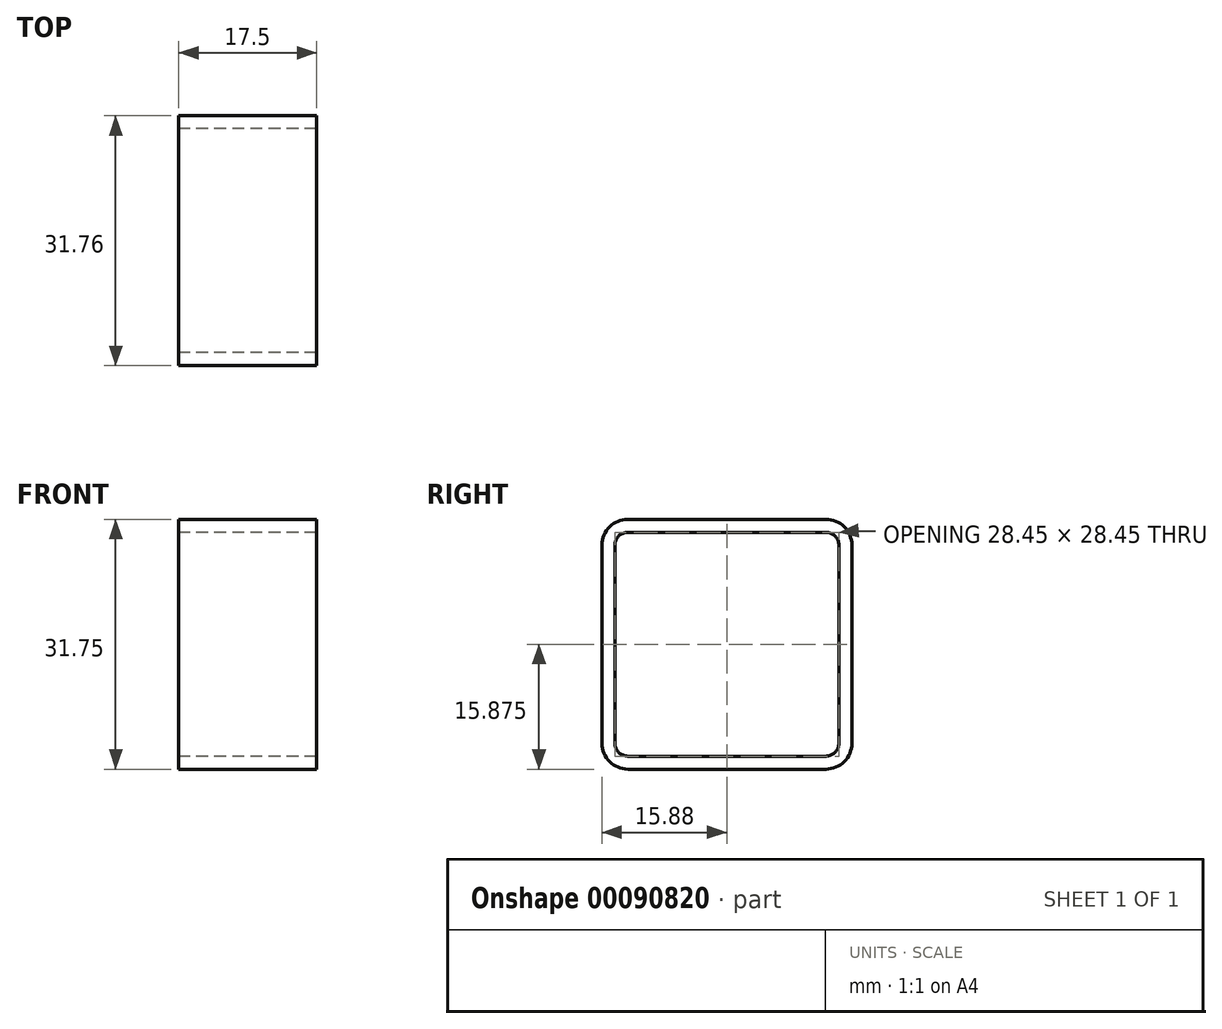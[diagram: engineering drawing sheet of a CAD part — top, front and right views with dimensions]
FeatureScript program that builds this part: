
annotation { "Feature Type Name" : "Feature", "Feature Type Description" : "" }
export const myFeature = defineFeature(function(context is Context, id is Id, definition is map)
    precondition{}
    {
        {
            var Q0;
            Q0=qCreatedBy(makeId("Top.planeOp"),FACE);
            var sketch = newSketch(context, id + "F0", { "sketchPlane" : qUnion([Q0])});
            skLineSegment(sketch, "E0.bottom", {"start": v(12.57, -15.88) * mm, "end": v(-12.57, -15.88) * mm});
            skLineSegment(sketch, "E0.top", {"start": v(12.57, 15.88) * mm, "end": v(-12.57, 15.88) * mm});
            skLineSegment(sketch, "E0.left", {"start": v(15.88, -12.57) * mm, "end": v(15.88, 12.57) * mm});
            skLineSegment(sketch, "E0.right", {"start": v(-15.88, -12.57) * mm, "end": v(-15.88, 12.57) * mm});
            skPoint(sketch, "E0.middle", {"position": v(0, 0) * mm});
            skPoint(sketch, "E1.visualSharp", {"position": v(-15.88, 15.87) * mm});
            skArc(sketch, "E1.filletArc", {"start": v(-12.57, 15.88) * mm, "mid": v(-14.9, 14.9) * mm, "end": v(-15.88, 12.57) * mm});
            skPoint(sketch, "E2.visualSharp", {"position": v(15.88, 15.88) * mm});
            skArc(sketch, "E2.filletArc", {"start": v(15.88, 12.57) * mm, "mid": v(14.9, 14.9) * mm, "end": v(12.57, 15.88) * mm});
            skPoint(sketch, "E3.visualSharp", {"position": v(15.87, -15.88) * mm});
            skArc(sketch, "E3.filletArc", {"start": v(12.57, -15.88) * mm, "mid": v(14.9, -14.9) * mm, "end": v(15.88, -12.57) * mm});
            skPoint(sketch, "E4.visualSharp", {"position": v(-15.88, -15.88) * mm});
            skArc(sketch, "E4.filletArc", {"start": v(-15.88, -12.57) * mm, "mid": v(-14.9, -14.9) * mm, "end": v(-12.57, -15.88) * mm});
            skLineSegment(sketch, "E5.0", {"start": v(12.57, 14.22) * mm, "end": v(-12.57, 14.22) * mm});
            skLineSegment(sketch, "E6.0", {"start": v(-14.22, -12.57) * mm, "end": v(-14.22, 12.57) * mm});
            skLineSegment(sketch, "E7.0", {"start": v(14.22, -12.57) * mm, "end": v(14.22, 12.57) * mm});
            skLineSegment(sketch, "E8.0", {"start": v(12.57, -14.22) * mm, "end": v(-12.57, -14.22) * mm});
            skArc(sketch, "E9.filletArc", {"start": v(-12.57, 14.22) * mm, "mid": v(-13.74, 13.74) * mm, "end": v(-14.22, 12.57) * mm});
            skArc(sketch, "E10.filletArc", {"start": v(14.22, 12.57) * mm, "mid": v(13.74, 13.74) * mm, "end": v(12.57, 14.22) * mm});
            skArc(sketch, "E11.filletArc", {"start": v(-14.22, -12.57) * mm, "mid": v(-13.74, -13.74) * mm, "end": v(-12.57, -14.22) * mm});
            skArc(sketch, "E12.filletArc", {"start": v(12.57, -14.22) * mm, "mid": v(13.74, -13.74) * mm, "end": v(14.22, -12.57) * mm});
            skSolve(sketch);
        }
        {
            assignVariable(context, id + "F1", {"name" : "L", "anyValue" : 17.5});
        }
        {
            var Q0;
            Q0=makeQuery(id+"F0.imprint","IMPRINT",FACE,{"disambiguationData":[TD([[makeQuery(id+"F0.imprint","IMPRINT",EDGE,{"derivedFrom":sQuery(id+"F0.wireOp",EDGE,"E0.bottom")}),-1.0]])]});
            extrude(context, id + "F2", {"entities" : qUnion([Q0]), "depth" : (getVariable(context, 'L')) * mm});
        }
        {
            var Q0;
            Q0=makeQuery(id+"F2.opExtrude","SWEPT_BODY",BODY,{"disambiguationData":[OSD([sQuery(id+"F0.wireOp",EDGE,"E0.bottom"),sQuery(id+"F0.wireOp",EDGE,"E0.top"),sQuery(id+"F0.wireOp",EDGE,"E0.left"),sQuery(id+"F0.wireOp",EDGE,"E0.right"),sQuery(id+"F0.wireOp",EDGE,"E1.filletArc"),sQuery(id+"F0.wireOp",EDGE,"E2.filletArc"),sQuery(id+"F0.wireOp",EDGE,"E3.filletArc"),sQuery(id+"F0.wireOp",EDGE,"E4.filletArc"),sQuery(id+"F0.wireOp",EDGE,"E5.0"),sQuery(id+"F0.wireOp",EDGE,"E6.0"),sQuery(id+"F0.wireOp",EDGE,"E7.0"),sQuery(id+"F0.wireOp",EDGE,"E8.0"),sQuery(id+"F0.wireOp",EDGE,"E9.filletArc"),sQuery(id+"F0.wireOp",EDGE,"E10.filletArc"),sQuery(id+"F0.wireOp",EDGE,"E11.filletArc"),sQuery(id+"F0.wireOp",EDGE,"E12.filletArc")])]});
            var Q1;
            Q1=makeQuery(id+"F2.opExtrude","CAP_EDGE",EDGE,{"disambiguationData":[OSD([sQuery(id+"F0.wireOp",EDGE,"E0.right")])],"isStart":false});
            var Q2;
            Q2=makeQuery(id+"F2.opExtrude","CAP_EDGE",EDGE,{"disambiguationData":[OSD([sQuery(id+"F0.wireOp",EDGE,"E0.right")])],"isStart":false});
            transform(context, id + "F3", {"entities" : qUnion([Q0]), "transformType" : TransformType.ROTATION, "transformAxis" : qUnion([Q2]), "angle" : 90 * degree, "makeCopy" : false});
        }
        {
            var Q0;
            Q0=makeQuery(id+"F2.opExtrude","SWEPT_FACE",FACE,{"disambiguationData":[OSD([sQuery(id+"F0.wireOp",EDGE,"E0.right")])]});
            var sketch = newSketch(context, id + "F4", { "sketchPlane" : qUnion([Q0])});
            skPoint(sketch, "E13", {"position": v(-365.13, 0) * mm});
            skPoint(sketch, "E14", {"position": v(-111.12, 0) * mm});
            skSolve(sketch);
        }
        {
            var Q0;
            Q0=sQuery(id+"F4.wireOp",VERTEX,"E13");
            var Q1;
            Q1=sQuery(id+"F4.wireOp",VERTEX,"E14");
            var Q2;
            Q2=makeQuery(id+"F2.opExtrude","SWEPT_BODY",BODY,{"disambiguationData":[OSD([sQuery(id+"F0.wireOp",EDGE,"E0.bottom"),sQuery(id+"F0.wireOp",EDGE,"E0.top"),sQuery(id+"F0.wireOp",EDGE,"E0.left"),sQuery(id+"F0.wireOp",EDGE,"E0.right"),sQuery(id+"F0.wireOp",EDGE,"E1.filletArc"),sQuery(id+"F0.wireOp",EDGE,"E2.filletArc"),sQuery(id+"F0.wireOp",EDGE,"E3.filletArc"),sQuery(id+"F0.wireOp",EDGE,"E4.filletArc"),sQuery(id+"F0.wireOp",EDGE,"E5.0"),sQuery(id+"F0.wireOp",EDGE,"E6.0"),sQuery(id+"F0.wireOp",EDGE,"E7.0"),sQuery(id+"F0.wireOp",EDGE,"E8.0"),sQuery(id+"F0.wireOp",EDGE,"E9.filletArc"),sQuery(id+"F0.wireOp",EDGE,"E10.filletArc"),sQuery(id+"F0.wireOp",EDGE,"E11.filletArc"),sQuery(id+"F0.wireOp",EDGE,"E12.filletArc")])]});
            hole(context, id + "F5", {"style" : HoleStyle.SIMPLE, "endStyle" : HoleEndStyle.THROUGH, "holeDiameter" : 7.94 * mm, "locations" : qUnion([Q0, Q1]), "scope" : qUnion([Q2]), "isTappedThrough" : true});
        }
        {
            var Q0;
            Q0=makeQuery(id+"F2.opExtrude","SWEPT_FACE",FACE,{"disambiguationData":[OSD([sQuery(id+"F0.wireOp",EDGE,"E0.right")])]});
            var sketch = newSketch(context, id + "F6", { "sketchPlane" : qUnion([Q0])});
            skPoint(sketch, "E15", {"position": v(-412.75, -4.76) * mm});
            skPoint(sketch, "E16", {"position": v(-63.5, -4.76) * mm});
            skSolve(sketch);
        }
    });
